# Revit family: 206_Watter battery-_
name_source: partatom
category: Duct Accessories
revit_build: Autodesk Revit 2018 (Build: 20170223_1515(x64)
units: mm (PartAtom-declared; Revit-internal decimal feet)

## family parameters
Always vertical = Yes
Cut with Voids When Loaded = No
Part Type = Breaks Into
Round Connector Dimension = Use Diameter
Shared = No
Work Plane-Based = No

## types (2) — shared parameters
CAT0 = Yes
CB = 205 mm  [stored 0.672572 ft]
CBT2 = 103 mm  [stored 0.337927 ft]
CH = 205 mm  [stored 0.672572 ft]
Description = Water coil complete
H2D = 205 mm  [stored 0.672572 ft]
L = 350 mm  [stored 1.14829 ft]
L2D = 350 mm  [stored 1.14829 ft]
LT2 = 175 mm  [stored 0.574147 ft]
Manufacturer = Flexit
QmdConnectorList = 201;D;202;D
W2D = 205 mm  [stored 0.672572 ft]
magiPartTypeId = 206
magiProductFamilyId = Watter battery-*

## per-type parameters (varying)
| type | D | magiProductId |
| 160-14466 | 160 mm | Watter battery-160 |
| 200-14467 | 200 mm | Watter battery-200 |

note: column(s) folded — value = type name in every type: MC Product Code

note: [stored X ft] marks values corroborated as IEEE doubles in the binary element streams (Revit-internal decimal feet)

## geometry (parser evidence)
native form markers: Sweep x2
no freeform markers — native parametric forms only
